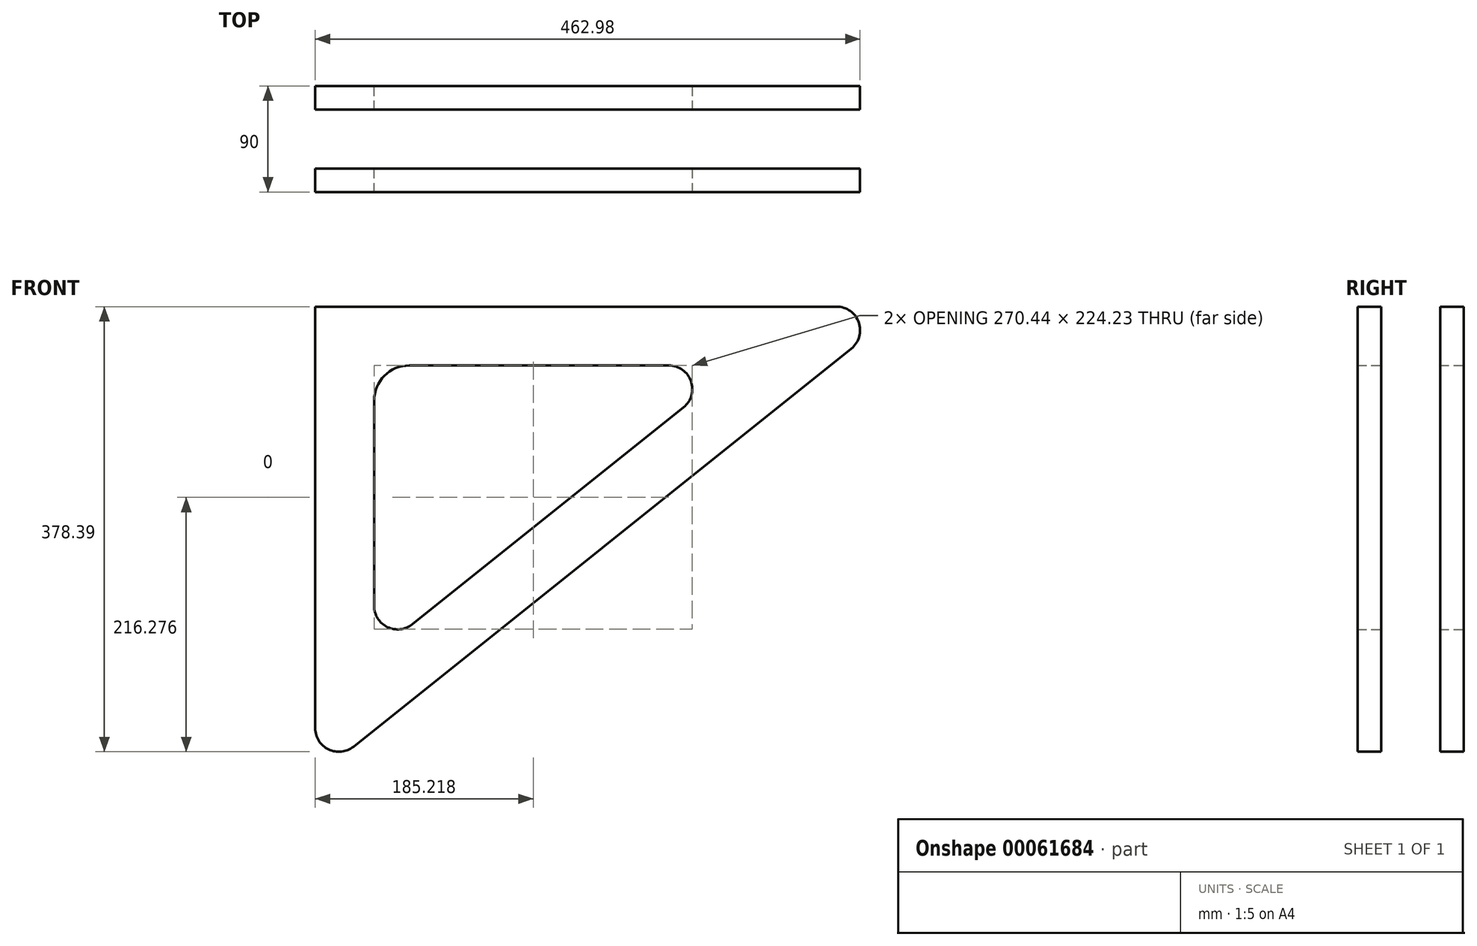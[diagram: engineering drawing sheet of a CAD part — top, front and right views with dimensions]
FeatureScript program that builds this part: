
annotation { "Feature Type Name" : "Feature", "Feature Type Description" : "" }
export const myFeature = defineFeature(function(context is Context, id is Id, definition is map)
    precondition{}
    {
        {
            var Q0;
            Q0=qCreatedBy(makeId("Front.planeOp"),FACE);
            var sketch = newSketch(context, id + "F0", { "sketchPlane" : qUnion([Q0])});
            skLineSegment(sketch, "E0", {"start": v(0, 0) * mm, "end": v(442.98, 0) * mm});
            skLineSegment(sketch, "E1", {"start": v(455.48, -35.62) * mm, "end": v(32.5, -374) * mm});
            skLineSegment(sketch, "E2", {"start": v(0, -358.39) * mm, "end": v(0, 0) * mm});
            skLineSegment(sketch, "E3.0", {"start": v(50, -254.36) * mm, "end": v(50, -80) * mm});
            skLineSegment(sketch, "E3.1", {"start": v(312.94, -85.62) * mm, "end": v(82.5, -269.97) * mm});
            skLineSegment(sketch, "E3.2", {"start": v(80, -50) * mm, "end": v(300.45, -50) * mm});
            skPoint(sketch, "E4.visualSharp", {"position": v(50, -50) * mm});
            skArc(sketch, "E4.filletArc", {"start": v(80, -50) * mm, "mid": v(58.79, -58.79) * mm, "end": v(50, -80) * mm});
            skPoint(sketch, "E5.visualSharp", {"position": v(50, -295.97) * mm});
            skArc(sketch, "E5.filletArc", {"start": v(50, -254.36) * mm, "mid": v(61.34, -272.38) * mm, "end": v(82.5, -269.97) * mm});
            skPoint(sketch, "E6.visualSharp", {"position": v(357.46, -50) * mm});
            skArc(sketch, "E6.filletArc", {"start": v(312.94, -85.62) * mm, "mid": v(319.32, -63.38) * mm, "end": v(300.45, -50) * mm});
            skPoint(sketch, "E7.visualSharp", {"position": v(500, 0) * mm});
            skArc(sketch, "E8.filletArc", {"start": v(455.48, -35.62) * mm, "mid": v(461.86, -13.38) * mm, "end": v(442.98, 0) * mm});
            skPoint(sketch, "E9.visualSharp", {"position": v(0, -400) * mm});
            skArc(sketch, "E9.filletArc", {"start": v(0, -358.39) * mm, "mid": v(11.34, -376.41) * mm, "end": v(32.5, -374) * mm});
            skSolve(sketch);
        }
        {
            var Q0;
            Q0=makeQuery(id+"F0.imprint","IMPRINT",FACE,{"disambiguationData":[TD([[makeQuery(id+"F0.imprint","IMPRINT",EDGE,{"derivedFrom":sQuery(id+"F0.wireOp",EDGE,"E0")}),-1.0]])]});
            extrude(context, id + "F1", {"entities" : qUnion([Q0]), "depth" : 20 * mm});
        }
        {
            var Q0;
            Q0=makeQuery(id+"F1.opExtrude","SWEPT_BODY",BODY,{"disambiguationData":[OSD([sQuery(id+"F0.wireOp",EDGE,"E0"),sQuery(id+"F0.wireOp",EDGE,"E1"),sQuery(id+"F0.wireOp",EDGE,"E2"),sQuery(id+"F0.wireOp",EDGE,"E3.0"),sQuery(id+"F0.wireOp",EDGE,"E3.1"),sQuery(id+"F0.wireOp",EDGE,"E3.2"),sQuery(id+"F0.wireOp",EDGE,"E4.filletArc"),sQuery(id+"F0.wireOp",EDGE,"E5.filletArc"),sQuery(id+"F0.wireOp",EDGE,"E6.filletArc"),sQuery(id+"F0.wireOp",EDGE,"E8.filletArc"),sQuery(id+"F0.wireOp",EDGE,"E9.filletArc")])]});
            transform(context, id + "F2", {"entities" : qUnion([Q0]), "transformType" : TransformType.TRANSLATION_3D, "dx" : 0 * mm, "dy" : 70 * mm, "dz" : 0 * mm, "makeCopy" : true});
        }
    });
